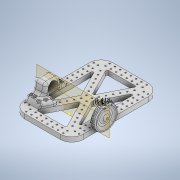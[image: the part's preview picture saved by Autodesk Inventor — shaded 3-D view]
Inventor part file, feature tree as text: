
AUTODESK INVENTOR PART (.ipt)
format: ipt  version: 2021 (Build 250183000, 183)  size: 1,823,744 bytes
history: native  units: mm
features: sketch x20, extrude x13, other x9, fillet x8, hole x4, pattern_linear x3, mirror x3, plane x2, pattern_circular x1
ambient origin geometry x8: Origin, YZ Plane, XZ Plane, XY Plane, X Axis, Y Axis, Z Axis, Center Point
bodies: Body1 (feature_tree), Body2 (feature_tree), Body3 (feature_tree), Body4 (feature_tree)
feature tree (63):
  other  "Chassis"
  extrude  "Extrusion1"  Depth=50.0mm
  fillet  "Fillet1"  Radius=9.0mm
  fillet  "Fillet2"  Radius=9.0mm
  sketch  "Sketch4"  dims[d18=9.0mm]
  hole  "Hole1"  [1 undecoded]
  pattern_linear  "Rectangular Pattern1"  Count1=2  [1 undecoded]
  sketch  "Sketch5"  dims[d19=9.0mm]
  hole  "Hole2"  [1 undecoded]
  pattern_linear  "Rectangular Pattern2"  Count1=2 Spacing1=7.0mm
  hole  "Hole3"  [1 undecoded]
  pattern_linear  "Rectangular Pattern3"  Count1=7 Spacing1=9.0mm
  mirror  "Mirror1"
  mirror  "Mirror2"
  extrude  "Extrusion2"  Depth=75.0mm
  extrude  "Extrusion4"  Depth=15.0mm
  extrude  "Extrusion5"  Depth=15.0mm
  extrude  "Extrusion6"  Depth=8.90625mm
  extrude  "Extrusion7"  Depth=10.0mm
  extrude  "Extrusion9"  Depth=2.0mm
  hole  "Hole5"  [1 undecoded]
  fillet  "Fillet3"  Radius=13.0mm
  fillet  "Fillet4"  Radius=20.0mm
  mirror  "Mirror3"
  extrude  "Extrusion10"  Depth=2.0mm TaperAngle=0.0deg
  extrude  "Extrusion11"  Depth=2.0mm
  extrude  "Extrusion13"  Depth=2.0mm TaperAngle=0.0deg
  extrude  "Extrusion15"  Depth=2.0mm
  extrude  "Extrusion16"  Depth=10.0mm
  fillet  "Fillet10"  Radius=12.0mm
  fillet  "Fillet11"  Radius=12.0mm
  fillet  "Fillet12"  Radius=18.0mm
  fillet  "Fillet13"  Radius=6.1mm
  other  "Work Point2"
  plane  "Work Plane1"
  extrude  "Extrusion17"  Depth=2.0mm TaperAngle=0.0deg
  pattern_circular  "Circular Pattern1"  Count=6  [1 undecoded]
  other  "Work Axis3"
  other  "Work Point3"
  plane  "Work Plane2"
  sketch  "Sketch27"  dims[d269=10.0mm d270=10.0mm d271=4.0mm d272=25.0mm d273=24.0mm d274=13.0mm d275=13.0mm d285=20.0mm d286=0.0mm d294=14.0mm d295=0.0mm d296=17.0mm d297=110.75mm d298=0.0mm d299=17.0mm d300=10.0mm d301=12.0mm d302=12.0mm d303=18.0mm d304=0.0mm d305=6.1mm d306=18.0mm d307=0.0mm d319=60.0mm d320=2.0mm d321=5.0mm d323=8.0mm d324=30.0mm d325=8.0mm d326=5.0mm d327=24.0mm d328=18.0mm d329=0.0mm d330=0.0mm d331=0.0mm d332=0.0mm d333=0.0mm d334=0.0mm d335=0.0mm d336=0.0mm d337=0.0mm d338=0.0mm d339=0.0mm d340=0.0mm d341=0.0mm d342=0.0mm d343=0.0mm d344=3.2mm d345=6.0mm d346=6.3mm d347=2.0mm d348=90.0deg d349=8.0mm d350=20.594885mm d351=25.0mm d352=25.0mm d353=5.0mm d354=2.0mm d355=12.0mm d356=0.0mm d357=40.0mm d358=10.0mm d359=0.0mm d371=1.5mm d372=4.0mm d373=0.0mm d374=8.0mm d375=0.0mm d380=3.0mm d381=2.0mm d382=3.5mm d383=0.0mm d384=0.0mm d385=0.0mm d386=3.5mm d387=0.0mm d388=5.0mm d389=5.0mm d390=5.0mm d391=1.0mm d401=1.0mm d402=-0.349066mm d403=400.0mm d404=360.0deg d427=0.2mm d428=0.2mm d429=0.4mm d430=0.4mm d432=1.5mm d433=2.5mm d434=1.0mm d435=1.0mm d436=1.752523mm d437=1.0mm d438=0.4175mm d439=0.417349mm d440=0.2mm]
  sketch  "Sketch1"  dims[d2=50.0mm d3=50.0mm d14=9.0mm d15=9.0mm]
  sketch  "Sketch3"  dims[d16=9.0mm d17=9.0mm]
  sketch  "Sketch6"  dims[d20=9.0mm]
  sketch  "Sketch7"  dims[d27=8.0mm d28=0.0mm]
  sketch  "Sketch8"  dims[d29=2.0mm d30=20.0mm]
  other  "Wheel Block Right"
  sketch  "Sketch10"  dims[d210=2.459mm d211=6.0mm d212=4.0mm d213=2.0mm d214=90.0deg d215=8.8mm d216=20.594885mm d219=40.0mm d221=-9.0mm]
  sketch  "Sketch11"  dims[d223=4.0mm]
  sketch  "Sketch12"  dims[d224=2.459mm d225=6.0mm d226=4.0mm d227=2.0mm d228=90.0deg d229=8.8mm d230=20.594885mm]
  sketch  "Sketch13"  dims[d231=4.5mm]
  sketch  "Sketch16"  dims[d232=4.0mm d233=20.0mm d235=7.0mm d236=4.5mm]
  sketch  "Sketch17"  dims[d237=70.0mm d239=9.0mm d240=20.0mm d242=7.0mm d243=4.5mm]
  other  "Pattern of Wheel Block Right:1"
  other  "Wheel Block Left"
  sketch  "Sketch18"  dims[d245=4.5mm]
  other  "Wheel"
  sketch  "Sketch19"  dims[d247=2.459mm d248=6.0mm d249=4.0mm d250=2.0mm d251=90.0deg d252=8.0mm d253=20.594885mm d254=70.0mm d256=9.0mm]
  sketch  "Sketch21"  dims[d257=75.0mm d258=75.0mm]
  sketch  "Sketch23"  dims[d259=15.0mm d260=15.0mm]
  sketch  "Sketch24"  dims[d261=15.0mm d262=15.0mm]
  sketch  "Sketch25"  dims[d263=9.0mm d264=8.90625mm]
  other  "Work Axis1"
note: 6 required parameter values undecoded (feature->parameter linkage not recoverable at this tier; creation-order binding heuristic only, values carry confidence <= 0.55)
